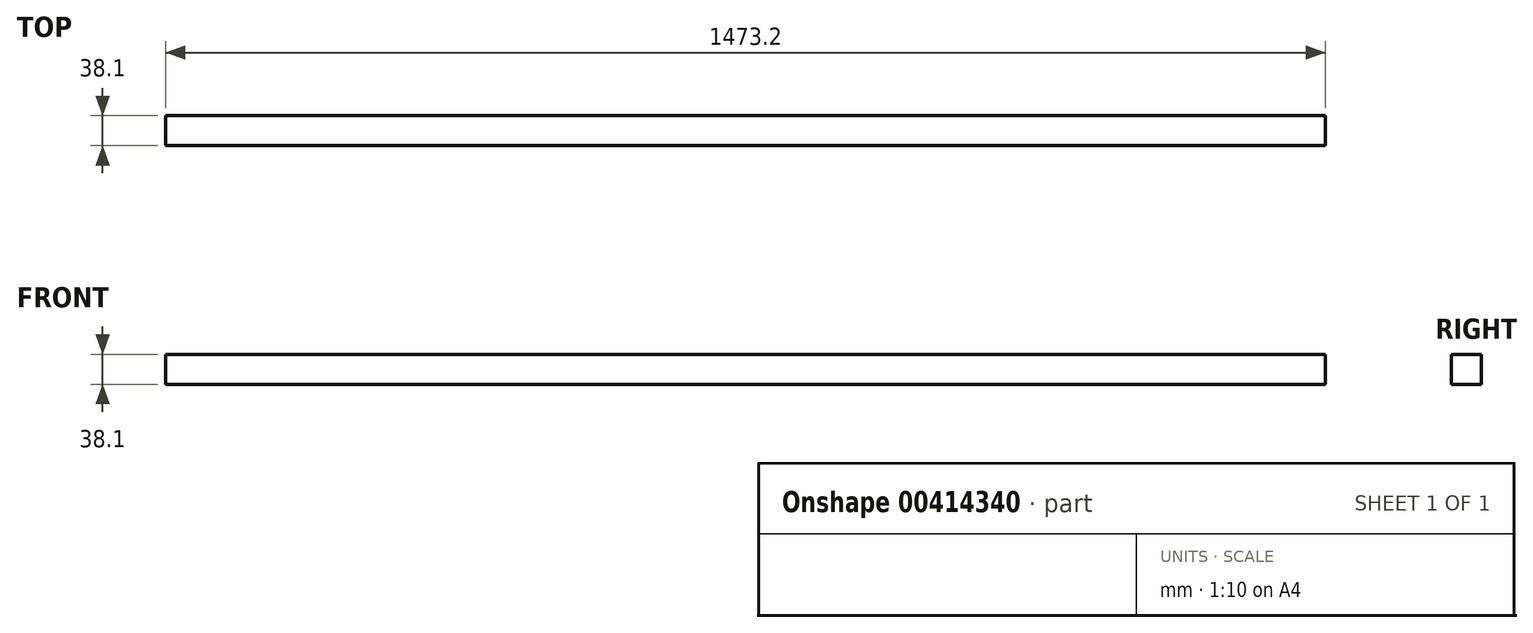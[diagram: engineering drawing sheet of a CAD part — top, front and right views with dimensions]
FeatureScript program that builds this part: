
annotation { "Feature Type Name" : "Feature", "Feature Type Description" : "" }
export const myFeature = defineFeature(function(context is Context, id is Id, definition is map)
    precondition{}
    {
        {
            var Q0;
            Q0=qCreatedBy(makeId("Top.planeOp"),FACE);
            var sketch = newSketch(context, id + "F0", { "sketchPlane" : qUnion([Q0])});
            skLineSegment(sketch, "E0.bottom", {"start": v(736.6, 19.05) * mm, "end": v(-736.6, 19.05) * mm});
            skLineSegment(sketch, "E0.top", {"start": v(736.6, -19.05) * mm, "end": v(-736.6, -19.05) * mm});
            skLineSegment(sketch, "E0.left", {"start": v(736.6, 19.05) * mm, "end": v(736.6, -19.05) * mm});
            skLineSegment(sketch, "E0.right", {"start": v(-736.6, 19.05) * mm, "end": v(-736.6, -19.05) * mm});
            skPoint(sketch, "E0.middle", {"position": v(0, 0) * mm});
            skSolve(sketch);
        }
        {
            var Q0;
            Q0 = qSketchRegion(id + "F0", true);
            extrude(context, id + "F1", {"entities" : qUnion([Q0]), "depth" : 38.1 * mm});
        }
    });
